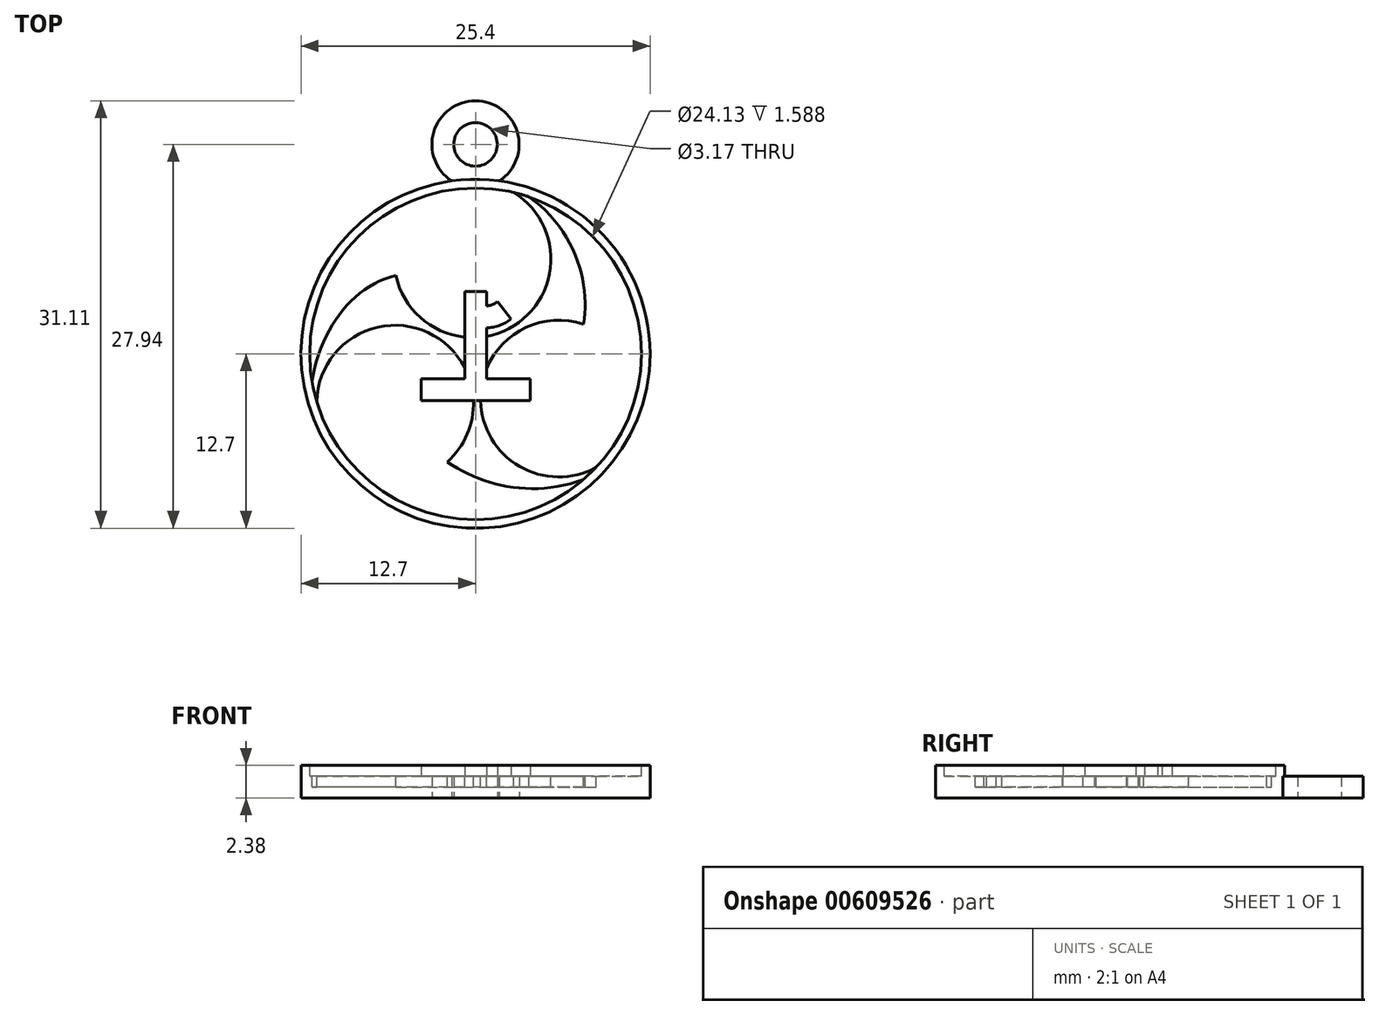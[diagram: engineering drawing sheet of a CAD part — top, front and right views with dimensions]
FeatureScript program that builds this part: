
annotation { "Feature Type Name" : "Feature", "Feature Type Description" : "" }
export const myFeature = defineFeature(function(context is Context, id is Id, definition is map)
    precondition{}
    {
        {
            var Q0;
            Q0=qCreatedBy(makeId("Top.planeOp"),FACE);
            var sketch = newSketch(context, id + "F0", { "sketchPlane" : qUnion([Q0])});
            skCircle(sketch, "E0", {"center": v(0, 0) * mm, "radius": 12.7 * mm});
            skSolve(sketch);
        }
        {
            var Q0;
            Q0 = qSketchRegion(id + "F0", true);
            extrude(context, id + "F1", {"entities" : qUnion([Q0]), "depth" : 1.59 * mm, "offsetDistance" : 25.4 * mm});
        }
        {
            var Q0;
            Q0=makeQuery(id+"F1.opExtrude","CAP_FACE",FACE,{"disambiguationData":[OSD([sQuery(id+"F0.wireOp",EDGE,"E0")])],"isStart":false});
            var sketch = newSketch(context, id + "F2", { "sketchPlane" : qUnion([Q0])});
            skLineSegment(sketch, "E1.bottom", {"start": v(12.7, 12.7) * mm, "end": v(-12.7, 12.7) * mm, "construction": true});
            skLineSegment(sketch, "E1.top", {"start": v(12.7, -12.7) * mm, "end": v(-12.7, -12.7) * mm, "construction": true});
            skLineSegment(sketch, "E1.left", {"start": v(12.7, 12.7) * mm, "end": v(12.7, -12.7) * mm, "construction": true});
            skLineSegment(sketch, "E1.right", {"start": v(-12.7, 12.7) * mm, "end": v(-12.7, -12.7) * mm, "construction": true});
            skPoint(sketch, "E1.middle", {"position": v(0, 0) * mm});
            skPoint(sketch, "E2", {"position": v(0, 12.7) * mm});
            skPoint(sketch, "E3", {"position": v(-12.7, 0) * mm});
            skCircle(sketch, "E4", {"center": v(0, 0) * mm, "radius": 12.7 * mm});
            skCircle(sketch, "E5", {"center": v(0, 0) * mm, "radius": 12.07 * mm});
            skArc(sketch, "E6", {"start": v(-5.8, 5.71) * mm, "mid": v(3.07, 2.22) * mm, "end": v(2.78, 11.74) * mm});
            skFitSpline(sketch, "E7", {"points": [v(-5.8, 5.71) * mm, v(-11.9, -1.97) * mm], "startDerivative": vector(-9.53, -2.38) * mm, "endDerivative": vector(-1.96, -11.44) * mm});
            skArc(sketch, "E8.1.0", {"start": v(-2.05, -7.87) * mm, "mid": v(-3.46, 1.55) * mm, "end": v(-11.56, -3.46) * mm});
            skArc(sketch, "E8.2.0", {"start": v(7.84, 2.16) * mm, "mid": v(0.39, -3.77) * mm, "end": v(8.78, -8.28) * mm});
            skFitSpline(sketch, "E9", {"points": [v(7.84, 2.16) * mm, v(3.88, 11.42) * mm], "startDerivative": vector(1.68, 8.53) * mm, "endDerivative": vector(-10.14, 7.03) * mm});
            skFitSpline(sketch, "E10", {"points": [v(-2.05, -7.87) * mm, v(7.84, -9.17) * mm], "startDerivative": vector(8.04, -5.42) * mm, "endDerivative": vector(11.06, 3.9) * mm});
            skSolve(sketch);
        }
        {
            var Q0;
            {var subQ0=sQuery(id+"F2.wireOp",EDGE,"E6");Q0=makeQuery(id+"F2.imprint","IMPRINT",FACE,{"disambiguationData":[TD([[makeQuery(id+"F2.imprint","IMPRINT",EDGE,{"derivedFrom":subQ0}),-1.0]])]});}
            extrude(context, id + "F3", {"entities" : qUnion([Q0]), "operationType" : NewBodyOperationType.REMOVE, "oppositeDirection" : true, "depth" : 0.8 * mm, "offsetDistance" : 25.4 * mm});
        }
        {
            var Q0;
            Q0=makeQuery(id+"F2.imprint","IMPRINT",FACE,{"disambiguationData":[TD([[makeQuery(id+"F2.imprint","IMPRINT",EDGE,{"derivedFrom":sQuery(id+"F2.wireOp",EDGE,"E4")}),1.0]])]});
            extrude(context, id + "F4", {"entities" : qUnion([Q0]), "operationType" : NewBodyOperationType.ADD, "depth" : 0.8 * mm, "offsetDistance" : 25.4 * mm});
        }
        {
            var Q0;
            {var subQ0=sQuery(id+"F2.wireOp",EDGE,"E6");Q0=makeQuery(id+"F4.boolean.opBoolean","SPLIT",FACE,{"disambiguationData":[TD([makeQuery(id+"F3.boolean.opBoolean","COPY",FACE,{"derivedFrom":makeQuery(id+"F3.opExtrude","SWEPT_FACE",FACE,{"disambiguationData":[OSD([subQ0])]})})])],"derivedFrom":makeQuery(id+"F1.opExtrude","CAP_FACE",FACE,{"disambiguationData":[OSD([sQuery(id+"F0.wireOp",EDGE,"E0")])],"isStart":false})});}
            var sketch = newSketch(context, id + "F5", { "sketchPlane" : qUnion([Q0])});
            skLineSegment(sketch, "E11", {"start": v(-3.97, -3.4) * mm, "end": v(3.97, -3.4) * mm});
            skLineSegment(sketch, "E12", {"start": v(3.97, -3.4) * mm, "end": v(3.97, -1.82) * mm});
            skLineSegment(sketch, "E13", {"start": v(3.97, -1.82) * mm, "end": v(0.8, -1.82) * mm});
            skLineSegment(sketch, "E14", {"start": v(0.8, -1.82) * mm, "end": v(0.8, 4.53) * mm});
            skLineSegment(sketch, "E15", {"start": v(0.8, 4.53) * mm, "end": v(-0.8, 4.53) * mm});
            skLineSegment(sketch, "E16", {"start": v(-0.8, 4.53) * mm, "end": v(-0.8, -1.82) * mm});
            skLineSegment(sketch, "E17", {"start": v(-0.8, -1.82) * mm, "end": v(-3.97, -1.82) * mm});
            skLineSegment(sketch, "E18", {"start": v(-3.97, -1.82) * mm, "end": v(-3.97, -3.4) * mm});
            skArc(sketch, "E19", {"start": v(0.8, 3.48) * mm, "mid": v(1.22, 3.57) * mm, "end": v(1.6, 3.8) * mm});
            skArc(sketch, "E20", {"start": v(0.8, 1.88) * mm, "mid": v(1.74, 2.06) * mm, "end": v(2.58, 2.53) * mm});
            skLineSegment(sketch, "E21", {"start": v(1.6, 3.8) * mm, "end": v(2.58, 2.53) * mm});
            skPoint(sketch, "E22", {"position": v(0, -3.4) * mm});
            skSolve(sketch);
        }
        {
            var Q0;
            Q0 = qSketchRegion(id + "F5", true);
            extrude(context, id + "F6", {"entities" : qUnion([Q0]), "operationType" : NewBodyOperationType.ADD, "depth" : 0.8 * mm, "offsetDistance" : 25.4 * mm, "hasSecondDirection" : true, "secondDirectionBound" : SecondDirectionBoundingType.UP_TO_NEXT, "secondDirectionOppositeDirection" : true, "secondDirectionDepth" : 25.4 * mm});
        }
        {
            var Q0;
            Q0=qCreatedBy(makeId("Top.planeOp"),FACE);
            var sketch = newSketch(context, id + "F7", { "sketchPlane" : qUnion([Q0])});
            skCircle(sketch, "E23", {"center": v(0, 15.24) * mm, "radius": 3.18 * mm});
            skCircle(sketch, "E24", {"center": v(0, 15.24) * mm, "radius": 1.59 * mm});
            skPoint(sketch, "E25", {"position": v(0, 12.07) * mm});
            skSolve(sketch);
        }
        {
            var Q0;
            Q0 = qSketchRegion(id + "F7", true);
            extrude(context, id + "F8", {"entities" : qUnion([Q0]), "operationType" : NewBodyOperationType.ADD, "depth" : 1.59 * mm, "offsetDistance" : 25.4 * mm});
        }
    });
